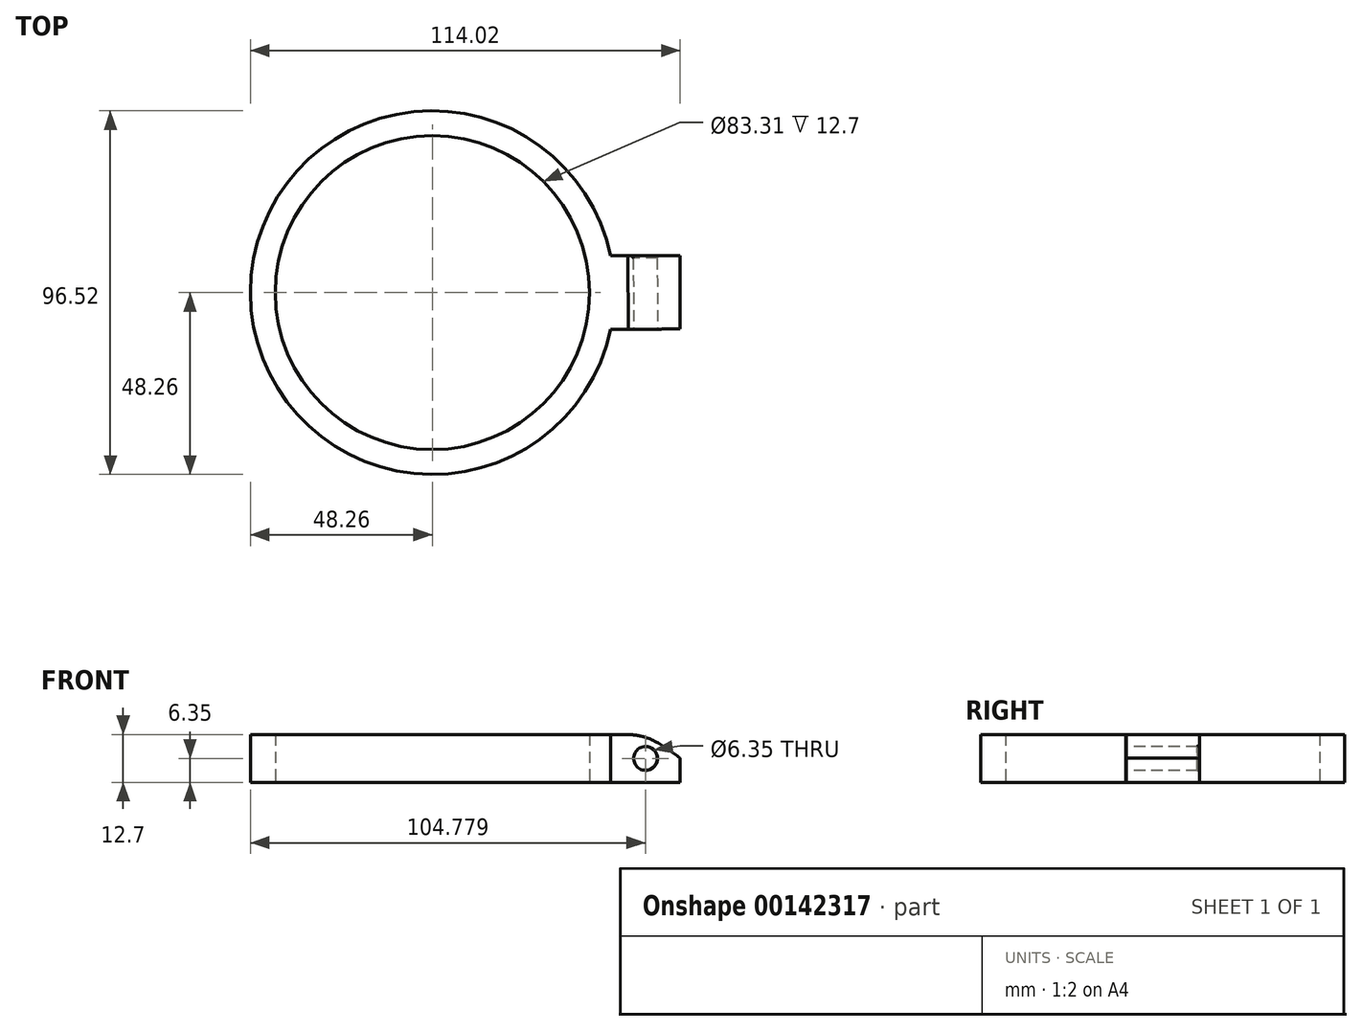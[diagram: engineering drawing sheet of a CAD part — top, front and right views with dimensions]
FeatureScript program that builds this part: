
annotation { "Feature Type Name" : "Feature", "Feature Type Description" : "" }
export const myFeature = defineFeature(function(context is Context, id is Id, definition is map)
    precondition{}
    {
        {
            var Q0;
            Q0=qCreatedBy(makeId("Top.planeOp"),FACE);
            var sketch = newSketch(context, id + "F0", { "sketchPlane" : qUnion([Q0])});
            skCircle(sketch, "E0", {"center": v(0, 0) * mm, "radius": 41.66 * mm});
            skCircle(sketch, "E1", {"center": v(0, 0) * mm, "radius": 48.26 * mm});
            skLineSegment(sketch, "E2", {"start": v(0, 0) * mm, "end": v(0, 12.7) * mm});
            skLineSegment(sketch, "E3", {"start": v(0, 0) * mm, "end": v(0, -12.7) * mm});
            skPoint(sketch, "E4", {"position": v(40.49, 9.8) * mm});
            skPoint(sketch, "E5", {"position": v(47.28, 9.65) * mm});
            skPoint(sketch, "E6", {"position": v(40.49, -9.8) * mm});
            skPoint(sketch, "E7", {"position": v(47.28, -9.65) * mm});
            skLineSegment(sketch, "E8", {"start": v(40.49, 9.8) * mm, "end": v(65.89, 9.8) * mm});
            skLineSegment(sketch, "E9", {"start": v(65.89, 9.8) * mm, "end": v(65.89, -9.65) * mm});
            skLineSegment(sketch, "E10", {"start": v(65.89, -9.65) * mm, "end": v(40.49, -9.8) * mm});
            skSolve(sketch);
        }
        {
            var Q0;
            {var subQ0=sQuery(id+"F0.wireOp",EDGE,"E8");var subQ1=sQuery(id+"F0.wireOp",EDGE,"E0");var subQ2=makeQuery(id+"F0.imprint","INTERSECT",VERTEX,{"derivedFrom":[subQ1,subQ0]});Q0=makeQuery(id+"F0.imprint","IMPRINT",FACE,{"disambiguationData":[TD([[makeQuery(id+"F0.imprint","IMPRINT",EDGE,{"disambiguationData":[TD([[subQ2,-1.0]])],"derivedFrom":subQ1}),-1.0]])]});}
            var Q1;
            {var subQ0=sQuery(id+"F0.wireOp",EDGE,"E8");var subQ1=sQuery(id+"F0.wireOp",EDGE,"E0");var subQ2=makeQuery(id+"F0.imprint","INTERSECT",VERTEX,{"derivedFrom":[subQ1,subQ0]});Q1=makeQuery(id+"F0.imprint","IMPRINT",FACE,{"disambiguationData":[TD([[makeQuery(id+"F0.imprint","IMPRINT",EDGE,{"disambiguationData":[TD([[subQ2,1.0]])],"derivedFrom":subQ1}),-1.0]])]});}
            var Q2;
            {var subQ5=sQuery(id+"F0.wireOp",EDGE,"E9");Q2=makeQuery(id+"F0.imprint","IMPRINT",FACE,{"disambiguationData":[TD([[makeQuery(id+"F0.imprint","IMPRINT",EDGE,{"derivedFrom":subQ5}),-1.0]])]});}
            extrude(context, id + "F1", {"entities" : qUnion([Q0, Q1, Q2]), "depth" : 12.7 * mm});
        }
        {
            var Q0;
            Q0=makeQuery(id+"F1.opExtrude","SWEPT_FACE",FACE,{"disambiguationData":[OSD([sQuery(id+"F0.wireOp",EDGE,"E10")])]});
            var sketch = newSketch(context, id + "F2", { "sketchPlane" : qUnion([Q0])});
            skPoint(sketch, "E11", {"position": v(56.52, 12.7) * mm});
            skPoint(sketch, "E12", {"position": v(65.83, 6.35) * mm});
            skCircle(sketch, "E13", {"center": v(56.52, 6.35) * mm, "radius": 3.18 * mm});
            skPoint(sketch, "E14", {"position": v(56.52, 11.11) * mm});
            skPoint(sketch, "E15", {"position": v(62.76, 6.35) * mm});
            skLineSegment(sketch, "E16", {"start": v(56.52, 11.11) * mm, "end": v(56.52, 12.7) * mm});
            skPoint(sketch, "E17", {"position": v(56.52, 11.9) * mm});
            skFitSpline(sketch, "E18", {"points": [v(47.2, 12.7) * mm, v(56.52, 11.9) * mm, v(65.83, 6.35) * mm], "startDerivative": vector(19.68, 0.53) * mm, "endDerivative": vector(17.6, -13.07) * mm});
            skSolve(sketch);
        }
        {
            var Q0;
            Q0=makeQuery(id+"F2.imprint","IMPRINT",FACE,{"disambiguationData":[TD([[makeQuery(id+"F2.imprint","IMPRINT",EDGE,{"derivedFrom":sQuery(id+"F2.wireOp",EDGE,"d2aa77df-eaf8-49da-8183-c04593320cd8")}),1.0]])]});
            var Q1;
            Q1=makeQuery(id+"F2.imprint","IMPRINT",FACE,{"disambiguationData":[TD([[makeQuery(id+"F2.imprint","IMPRINT",EDGE,{"derivedFrom":sQuery(id+"F2.wireOp",EDGE,"E13")}),1.0]])]});
            extrude(context, id + "F3", {"entities" : qUnion([Q0, Q1]), "operationType" : NewBodyOperationType.REMOVE, "oppositeDirection" : true, "depth" : 25.4 * mm});
        }
        {
            var Q0;
            Q0=makeQuery(id+"F1.opExtrude","SWEPT_FACE",FACE,{"disambiguationData":[OSD([sQuery(id+"F0.wireOp",EDGE,"E9")])]});
            extrude(context, id + "F4", {"entities" : qUnion([Q0]), "operationType" : NewBodyOperationType.REMOVE, "oppositeDirection" : true, "depth" : 0.13 * mm});
        }
        {
            var Q0;
            Q0=makeQuery(id+"F3.boolean.opBoolean","COPY",EDGE,{"derivedFrom":makeQuery(id+"F3.opExtrude","CAP_EDGE",EDGE,{"disambiguationData":[OSD([sQuery(id+"F2.wireOp",EDGE,"E13")])],"isStart":true})});
            var Q1;
            Q1=makeQuery(id+"F3.boolean.opBoolean","INTERSECT",EDGE,{"derivedFrom":[makeQuery(id+"F1.opExtrude","SWEPT_FACE",FACE,{"disambiguationData":[OSD([sQuery(id+"F0.wireOp",EDGE,"E8")])]}),makeQuery(id+"F3.opExtrude","SWEPT_FACE",FACE,{"disambiguationData":[OSD([sQuery(id+"F2.wireOp",EDGE,"E13")])]})]});
            fillet(context, id + "F5", {"entities" : qUnion([Q0, Q1]), "radius" : 0.64 * mm, "tangentPropagation" : true, "rho" : .1, "crossSection" : FilletCrossSection.CONIC, "allowEdgeOverflow" : false});
        }
        {
            var Q0;
            {var subQ0=sQuery(id+"F2.wireOp",EDGE,"E16");var subQ1=sQuery(id+"F0.wireOp",EDGE,"E10");var subQ2=makeQuery(id+"F1.opExtrude","CAP_EDGE",EDGE,{"disambiguationData":[OSD([subQ1])],"isStart":false});var subQ3=makeQuery(id+"F2.imprint","INTERSECT",VERTEX,{"derivedFrom":[subQ2,subQ0]});Q0=makeQuery(id+"F2.imprint","IMPRINT",FACE,{"disambiguationData":[TD([[makeQuery(id+"F2.imprint","IMPRINT",EDGE,{"disambiguationData":[TD([[subQ3,1.0]])],"derivedFrom":subQ0}),-1.0]])]});}
            var Q1;
            {var subQ0=sQuery(id+"F2.wireOp",EDGE,"E16");var subQ1=makeQuery(id+"F1.opExtrude","CAP_EDGE",EDGE,{"disambiguationData":[OSD([sQuery(id+"F0.wireOp",EDGE,"E10")])],"isStart":false});var subQ2=makeQuery(id+"F2.imprint","INTERSECT",VERTEX,{"derivedFrom":[subQ1,subQ0]});Q1=makeQuery(id+"F2.imprint","IMPRINT",FACE,{"disambiguationData":[TD([[makeQuery(id+"F2.imprint","IMPRINT",EDGE,{"disambiguationData":[TD([[subQ2,1.0]])],"derivedFrom":subQ0}),1.0]])]});}
            extrude(context, id + "F6", {"entities" : qUnion([Q0, Q1]), "operationType" : NewBodyOperationType.REMOVE, "oppositeDirection" : true, "depth" : 25.4 * mm});
        }
    });
